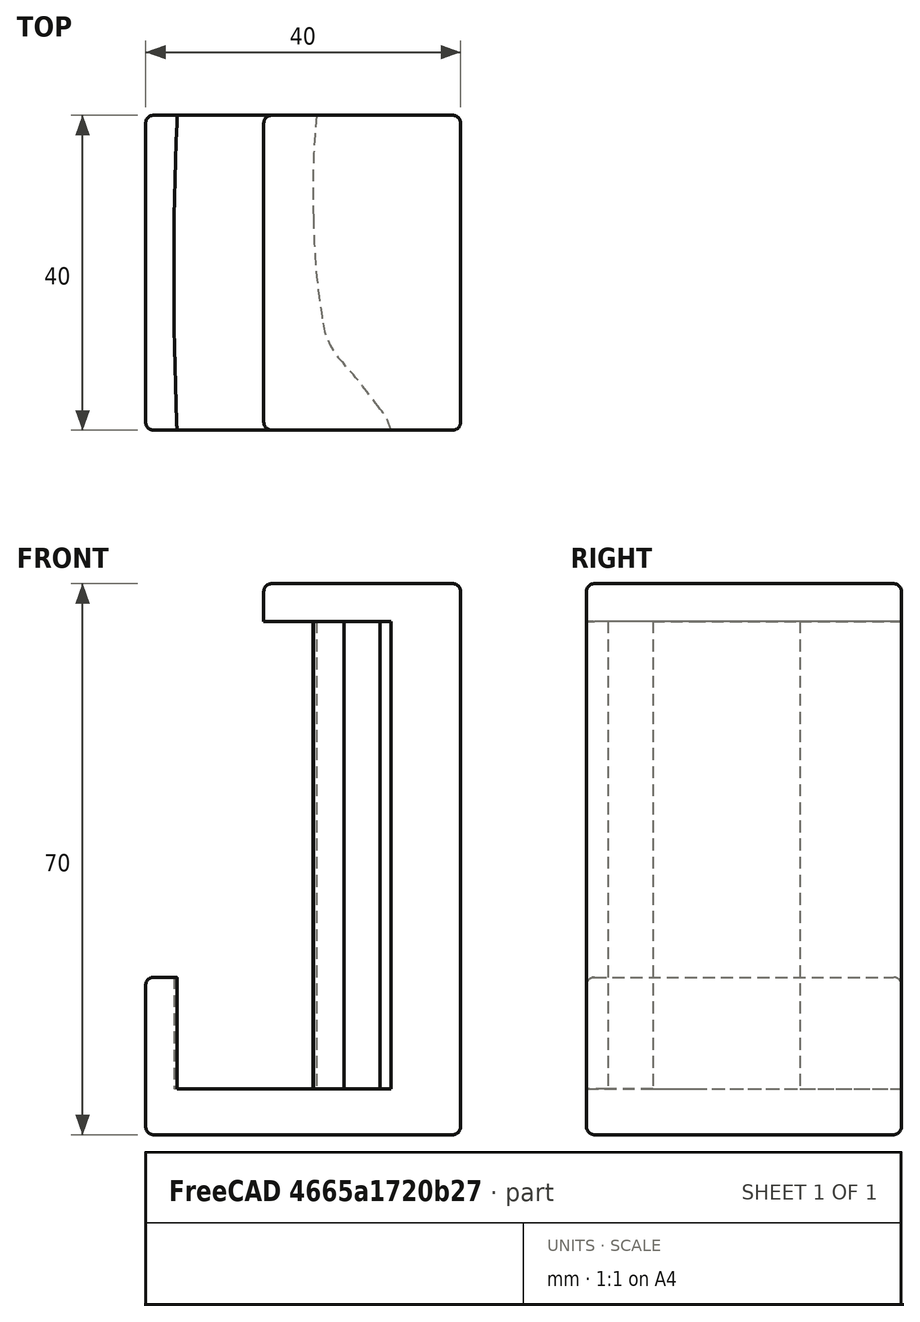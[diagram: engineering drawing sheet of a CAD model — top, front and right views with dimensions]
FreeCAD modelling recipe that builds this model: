
FCSTD DOCUMENT  (FreeCAD 0.18R16146 (Git))
Label: clicgear_bracket
License: All rights reserved
LicenseURL: http://en.wikipedia.org/wiki/All_rights_reserved
objects: Part::Box×3, Part::MultiFuse×2, Part::Cut×2, Image::ImagePlane×1, Sketcher::SketchObject×1, PartDesign::Pad×1, PartDesign::Body×1, Part::Offset×1, Part::FeaturePython×1, Part::Extrusion×1, Part::Fillet×1
note: 15 computed .brp shape members not serialized (recipe doc carries the construction recipe); baked Part::Feature solids carry a one-line shape summary decoded from their .brp

FEATURE [Image::ImagePlane] ImagePlane
  Placement = pos=(0,0,-1) rot=(0,0,1;0rad)
  XSize = 31.8
  YSize = 111
FEATURE [Sketcher::SketchObject] Sketch
  MapMode = 5
  Support = -> [XY_Plane]
  sketch-geometry (12):
    g0: ArcOfCircle CenterX=-4.64755 CenterY=-7.25034 CenterZ=0 NormalX=0 NormalY=0 NormalZ=1 AngleXU=0 Radius=59.1642 StartAngle=1.49391 EndAngle=1.63547
    g1: ArcOfCircle CenterX=-0.443655 CenterY=41.2464 CenterZ=0 NormalX=0 NormalY=0 NormalZ=1 AngleXU=0 Radius=10.4981 StartAngle=0.0444994 EndAngle=1.53836
    g2: ArcOfCircle CenterX=-4.49731 CenterY=41.4452 CenterZ=0 NormalX=0 NormalY=0 NormalZ=1 AngleXU=0 Radius=14.5438 StartAngle=5.92607 EndAngle=6.30163
    g3: ArcOfCircle CenterX=105.861 CenterY=4.58097 CenterZ=0 NormalX=0 NormalY=0 NormalZ=1 AngleXU=0 Radius=101.819 StartAngle=2.82416 EndAngle=3.17599
    g4: ArcOfCircle CenterX=95.0106 CenterY=2.37672 CenterZ=0 NormalX=0 NormalY=0 NormalZ=1 AngleXU=0 Radius=90.9174 StartAngle=3.15586 EndAngle=3.30502
    g5: ArcOfCircle CenterX=14.8686 CenterY=-10.8454 CenterZ=0 NormalX=0 NormalY=0 NormalZ=1 AngleXU=0 Radius=9.69196 StartAngle=3.30434 EndAngle=3.93098
    g6: ArcOfCircle CenterX=8.21809 CenterY=-27.3563 CenterZ=0 NormalX=0 NormalY=0 NormalZ=1 AngleXU=0 Radius=5.88399 StartAngle=5.56617 EndAngle=7.01518
    g7: ArcOfCircle CenterX=25.105 CenterY=-37.2383 CenterZ=0 NormalX=0 NormalY=0 NormalZ=1 AngleXU=0 Radius=13.8286 StartAngle=2.69156 EndAngle=3.28003
    g8: ArcOfCircle CenterX=-0.309604 CenterY=-39.9443 CenterZ=0 NormalX=0 NormalY=0 NormalZ=1 AngleXU=0 Radius=11.7454 StartAngle=3.27704 EndAngle=6.35116
    g9: ArcOfCircle CenterX=469.447 CenterY=-6.44146 CenterZ=0 NormalX=0 NormalY=0 NormalZ=1 AngleXU=0 Radius=482.672 StartAngle=3.02334 EndAngle=3.21435
    g10: ArcOfCircle CenterX=-8.35679 CenterY=50.2812 CenterZ=0 NormalX=0 NormalY=0 NormalZ=1 AngleXU=0 Radius=1.51329 StartAngle=1.64659 EndAngle=2.99459
    g11: ArcOfCircle CenterX=-47.3669 CenterY=-66.662 CenterZ=0 NormalX=0 NormalY=0 NormalZ=1 AngleXU=0 Radius=73.9254 StartAngle=0.624746 EndAngle=0.723438
  constraints (12):
    c: Coincident(g1,g0)
    c: Coincident(g2,g1)
    c: Coincident(g3,g2)
    c: Coincident(g4,g3)
    c: Coincident(g5,g4)
    c: Coincident(g7,g6)
    c: Coincident(g8,g7)
    c: Coincident(g9,g8)
    c: Coincident(g10,g9)
    c: Coincident(g10,g0)
    c: Coincident(g11,g5)
    c: Coincident(g11,g6)
FEATURE [PartDesign::Pad] Pad
  Length = 59
  Length2 = 100
  Profile = -> Sketch
  Type = 0
FEATURE [PartDesign::Body] Body  label="Clicgear bracket"
  Group = -> [Sketch,Pad]
  Origin = -> Origin
  Tip = -> Pad
FEATURE [Part::Box] Box  label="Cube"
  AttacherType = Attacher::AttachEngine3D
  Height = 20
  Length = 35
  Placement = pos=(-17,-26,-6) rot=(0,0,1;0rad)
  Width = 45
FEATURE [Part::Box] Box001  label="Cube001"
  AttacherType = Attacher::AttachEngine3D
  Height = 70
  Length = 23
  Placement = pos=(0,-26,-6) rot=(0,0,1;0rad)
  Width = 45
FEATURE [Part::MultiFuse] Fusion
  Shapes = -> [Box,Box001]
FEATURE [Part::Offset] Offset
  Fill = false
  Intersection = false
  Join = 2
  Mode = 0
  SelfIntersection = false
  Source = -> Body
  Value = 0.2
FEATURE [Part::Cut] Cut
  Base = -> Fusion
  Tool = -> Offset
FEATURE [Part::Box] Box002  label="Cube002"
  AttacherType = Attacher::AttachEngine3D
  Height = 70
  Length = 40
  Placement = pos=(-17,14,-6) rot=(0,0,1;0rad)
  Width = 5
FEATURE [Part::Cut] Cut001
  Base = -> Cut
  Tool = -> Box002
FEATURE [Part::FeaturePython] Facebinder  # WARN: FeaturePython — macro-defined, semantics opaque (R4)
  Extrusion = 0
  Faces = -> [Cut001]
  RemoveSplitter = false
  Sew = false
FEATURE [Part::Extrusion] Extrude
  Base = -> Facebinder
  Dir = (-1,0,0)
  DirMode = 2
  FaceMakerClass = Part::FaceMakerBullseye
  LengthFwd = 2
  LengthRev = 0
  Solid = false
  Symmetric = false
FEATURE [Part::MultiFuse] Fusion001
  Shapes = -> [Extrude,Cut001]
FEATURE [Part::Fillet] Fillet
  Base = -> Fusion001
  Edges = 23 edges r=1: [Edge2,Edge4,Edge8,Edge10,Edge11,Edge12,Edge13,Edge18,Edge26,Edge27,Edge28,Edge29,Edge31,Edge35,Edge38,Edge39,Edge43,Edge44,Edge55,Edge57,Edge58,Edge59,Edge61]
